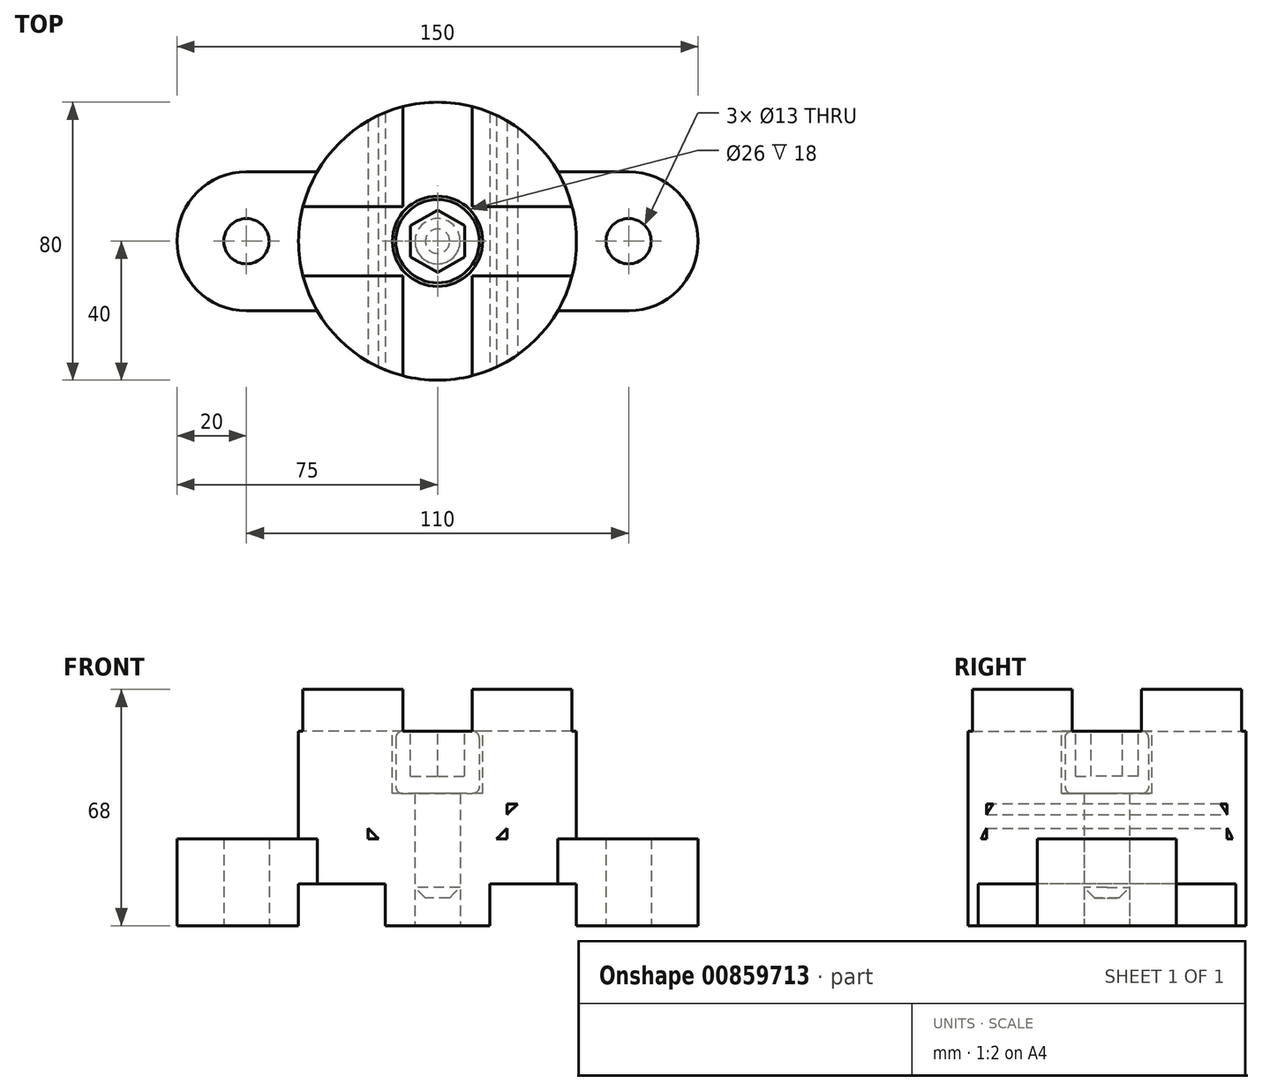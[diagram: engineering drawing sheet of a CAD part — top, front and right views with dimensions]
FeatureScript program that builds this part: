
annotation { "Feature Type Name" : "Feature", "Feature Type Description" : "" }
export const myFeature = defineFeature(function(context is Context, id is Id, definition is map)
    precondition{}
    {
        {
            var Q0;
            Q0=qCreatedBy(makeId("Top.planeOp"),FACE);
            var sketch = newSketch(context, id + "F0", { "sketchPlane" : qUnion([Q0])});
            skCircle(sketch, "E0", {"center": v(0, 0) * mm, "radius": 40 * mm});
            skArc(sketch, "E1", {"start": v(55, -20) * mm, "mid": v(75, 0) * mm, "end": v(55, 20) * mm});
            skArc(sketch, "E2", {"start": v(-55, 20) * mm, "mid": v(-75, 0) * mm, "end": v(-55, -20) * mm});
            skLineSegment(sketch, "E3", {"start": v(-55, 20) * mm, "end": v(55, 20) * mm});
            skLineSegment(sketch, "E4", {"start": v(-55, -20) * mm, "end": v(55, -20) * mm});
            skCircle(sketch, "E5", {"center": v(0, 0) * mm, "radius": 6.5 * mm});
            skCircle(sketch, "E6", {"center": v(-55, 0) * mm, "radius": 6.5 * mm});
            skCircle(sketch, "E7", {"center": v(55, 0) * mm, "radius": 6.5 * mm});
            skSolve(sketch);
        }
        {
            var Q0;
            {var subQ0=sQuery(id+"F0.wireOp",EDGE,"E4");var subQ1=sQuery(id+"F0.wireOp",EDGE,"E0");var subQ2=makeQuery(id+"F0.imprint","INTERSECT",VERTEX,{"disambiguationData":[OD(0.0)],"derivedFrom":[subQ1,subQ0]});Q0=makeQuery(id+"F0.imprint","IMPRINT",FACE,{"disambiguationData":[TD([[makeQuery(id+"F0.imprint","IMPRINT",EDGE,{"disambiguationData":[TD([[subQ2,-1.0]])],"derivedFrom":subQ1}),1.0]])]});}
            var Q1;
            Q1=makeQuery(id+"F0.imprint","IMPRINT",FACE,{"disambiguationData":[TD([[makeQuery(id+"F0.imprint","IMPRINT",EDGE,{"derivedFrom":sQuery(id+"F0.wireOp",EDGE,"E5")}),-1.0]])]});
            var Q2;
            {var subQ0=sQuery(id+"F0.wireOp",EDGE,"E3");var subQ1=sQuery(id+"F0.wireOp",EDGE,"E0");var subQ2=makeQuery(id+"F0.imprint","INTERSECT",VERTEX,{"disambiguationData":[OD(0.0)],"derivedFrom":[subQ1,subQ0]});Q2=makeQuery(id+"F0.imprint","IMPRINT",FACE,{"disambiguationData":[TD([[makeQuery(id+"F0.imprint","IMPRINT",EDGE,{"disambiguationData":[TD([[subQ2,1.0]])],"derivedFrom":subQ1}),1.0]])]});}
            extrude(context, id + "F1", {"entities" : qUnion([Q0, Q1, Q2]), "depth" : 35 * mm, "offsetDistance" : 25 * mm});
        }
        {
            var Q0;
            {var subQ1=sQuery(id+"F0.wireOp",EDGE,"E2");Q0=makeQuery(id+"F0.imprint","IMPRINT",FACE,{"disambiguationData":[TD([[makeQuery(id+"F0.imprint","IMPRINT",EDGE,{"derivedFrom":subQ1}),1.0]])]});}
            var Q1;
            {var subQ1=sQuery(id+"F0.wireOp",EDGE,"E1");Q1=makeQuery(id+"F0.imprint","IMPRINT",FACE,{"disambiguationData":[TD([[makeQuery(id+"F0.imprint","IMPRINT",EDGE,{"derivedFrom":subQ1}),1.0]])]});}
            extrude(context, id + "F2", {"entities" : qUnion([Q0, Q1]), "operationType" : NewBodyOperationType.ADD, "depth" : 25 * mm, "offsetDistance" : 25 * mm});
        }
        {
            var Q0;
            Q0=qCreatedBy(makeId("Front.planeOp"),FACE);
            var sketch = newSketch(context, id + "F3", { "sketchPlane" : qUnion([Q0])});
            skLineSegment(sketch, "E8.bottom", {"start": v(20, 35) * mm, "end": v(-20, 35) * mm});
            skLineSegment(sketch, "E8.top", {"start": v(20, 25) * mm, "end": v(-20, 25) * mm});
            skLineSegment(sketch, "E8.left", {"start": v(20, 35) * mm, "end": v(20, 25) * mm});
            skLineSegment(sketch, "E8.right", {"start": v(-20, 35) * mm, "end": v(-20, 25) * mm});
            skPoint(sketch, "E8.middle", {"position": v(0, 30) * mm});
            skLineSegment(sketch, "E9.bottom", {"start": v(-40, 0) * mm, "end": v(-15, 0) * mm});
            skLineSegment(sketch, "E9.top", {"start": v(-40, 12) * mm, "end": v(-15, 12) * mm});
            skLineSegment(sketch, "E9.left", {"start": v(-40, 0) * mm, "end": v(-40, 12) * mm});
            skLineSegment(sketch, "E9.right", {"start": v(-15, 0) * mm, "end": v(-15, 12) * mm});
            skLineSegment(sketch, "E10.bottom", {"start": v(15, 0) * mm, "end": v(40, 0) * mm});
            skLineSegment(sketch, "E10.top", {"start": v(15, 12) * mm, "end": v(40, 12) * mm});
            skLineSegment(sketch, "E10.left", {"start": v(15, 0) * mm, "end": v(15, 12) * mm});
            skLineSegment(sketch, "E10.right", {"start": v(40, 0) * mm, "end": v(40, 12) * mm});
            skSolve(sketch);
        }
        {
            var Q0;
            Q0 = qSketchRegion(id + "F3", true);
            extrude(context, id + "F4", {"entities" : qUnion([Q0]), "operationType" : NewBodyOperationType.REMOVE, "endBound" : BoundingType.SYMMETRIC, "oppositeDirection" : true, "depth" : 100 * mm, "offsetDistance" : 25 * mm});
        }
        {
            var Q0;
            Q0=makeQuery(id+"F4.boolean.opBoolean","COPY",EDGE,{"derivedFrom":makeQuery(id+"F4.opExtrude","SWEPT_EDGE",EDGE,{"disambiguationData":[OSD([sQuery(id+"F3.wireOp",EDGE,"E8.bottom"),sQuery(id+"F3.wireOp",EDGE,"E8.right")])]})});
            var Q1;
            Q1=makeQuery(id+"F4.boolean.opBoolean","COPY",EDGE,{"derivedFrom":makeQuery(id+"F4.opExtrude","SWEPT_EDGE",EDGE,{"disambiguationData":[OSD([sQuery(id+"F3.wireOp",EDGE,"E8.bottom"),sQuery(id+"F3.wireOp",EDGE,"E8.left")])]})});
            chamfer(context, id + "F5", {"entities" : qUnion([Q0, Q1]), "width" : 3 * mm, "tangentPropagation" : true});
        }
        {
            var Q0;
            Q0=makeQuery(id+"F4.boolean.opBoolean","COPY",FACE,{"derivedFrom":makeQuery(id+"F4.opExtrude","SWEPT_FACE",FACE,{"disambiguationData":[OSD([sQuery(id+"F3.wireOp",EDGE,"E8.top")])]})});
            var sketch = newSketch(context, id + "F6", { "sketchPlane" : qUnion([Q0])});
            skArc(sketch, "E11.0", {"start": v(20, 34.64) * mm, "mid": v(0, 40) * mm, "end": v(-20, 34.64) * mm});
            skCircle(sketch, "E11.1", {"center": v(0, 0) * mm, "radius": 6.5 * mm});
            skLineSegment(sketch, "E11.2", {"start": v(-20, 34.64) * mm, "end": v(-20, -34.64) * mm});
            skArc(sketch, "E11.3", {"start": v(-20, -34.64) * mm, "mid": v(0, -40) * mm, "end": v(20, -34.64) * mm});
            skLineSegment(sketch, "E11.4", {"start": v(20, 34.64) * mm, "end": v(20, -34.64) * mm});
            skSolve(sketch);
        }
        {
            var Q0;
            Q0 = qSketchRegion(id + "F6", true);
            var Q1;
            {var subQ0=sQuery(id+"F0.wireOp",EDGE,"E0");Q1=makeQuery(id+"F4.boolean.opBoolean","SPLIT",FACE,{"disambiguationData":[TD([makeQuery(id+"F4.opExtrude","SWEPT_FACE",FACE,{"disambiguationData":[OSD([sQuery(id+"F3.wireOp",EDGE,"E8.right")])]})])],"derivedFrom":makeQuery(id+"F1.opExtrude","CAP_FACE",FACE,{"disambiguationData":[OSD([subQ0,sQuery(id+"F0.wireOp",EDGE,"E5")])],"isStart":false})});}
            extrude(context, id + "F7", {"entities" : qUnion([Q0]), "endBound" : BoundingType.UP_TO_SURFACE, "depth" : 25 * mm, "endBoundEntityFace" : qUnion([Q1]), "offsetDistance" : 25 * mm});
        }
        {
            var Q0;
            Q0=makeQuery(id+"F7.opExtrude","CAP_EDGE",EDGE,{"disambiguationData":[OSD([sQuery(id+"F6.wireOp",EDGE,"E11.4")])],"isStart":true});
            var Q1;
            Q1=makeQuery(id+"F7.opExtrude","CAP_EDGE",EDGE,{"disambiguationData":[OSD([sQuery(id+"F6.wireOp",EDGE,"E11.2")])],"isStart":true});
            chamfer(context, id + "F8", {"entities" : qUnion([Q0, Q1]), "width" : 3 * mm, "tangentPropagation" : true});
        }
        {
            var Q0;
            Q0=makeQuery(id+"F7.opExtrude","CAP_FACE",FACE,{"disambiguationData":[OSD([sQuery(id+"F6.wireOp",EDGE,"E11.0"),sQuery(id+"F6.wireOp",EDGE,"E11.1"),sQuery(id+"F6.wireOp",EDGE,"E11.2"),sQuery(id+"F6.wireOp",EDGE,"E11.3"),sQuery(id+"F6.wireOp",EDGE,"E11.4")])],"isStart":false});
            var sketch = newSketch(context, id + "F9", { "sketchPlane" : qUnion([Q0])});
            skCircle(sketch, "E12", {"center": v(0, 0) * mm, "radius": 40 * mm});
            skSolve(sketch);
        }
        {
            var Q0;
            Q0 = qSketchRegion(id + "F9", true);
            extrude(context, id + "F10", {"entities" : qUnion([Q0]), "operationType" : NewBodyOperationType.ADD, "depth" : (45 - 12) * mm, "offsetDistance" : 25 * mm});
        }
        {
            var Q0;
            Q0=makeQuery(id+"F10.opExtrude","CAP_FACE",FACE,{"disambiguationData":[OSD([sQuery(id+"F9.wireOp",EDGE,"E12")])],"isStart":false});
            var sketch = newSketch(context, id + "F11", { "sketchPlane" : qUnion([Q0])});
            skCircle(sketch, "E13", {"center": v(0, 0) * mm, "radius": 13 * mm});
            skLineSegment(sketch, "E14.bottom", {"start": v(40, -10) * mm, "end": v(-40, -10) * mm});
            skLineSegment(sketch, "E14.top", {"start": v(40, 10) * mm, "end": v(-40, 10) * mm});
            skLineSegment(sketch, "E14.left", {"start": v(40, -10) * mm, "end": v(40, 10) * mm});
            skLineSegment(sketch, "E14.right", {"start": v(-40, -10) * mm, "end": v(-40, 10) * mm});
            skLineSegment(sketch, "E15.bottom", {"start": v(10, -40) * mm, "end": v(-10, -40) * mm});
            skLineSegment(sketch, "E15.top", {"start": v(10, 40) * mm, "end": v(-10, 40) * mm});
            skLineSegment(sketch, "E15.left", {"start": v(10, -40) * mm, "end": v(10, 40) * mm});
            skLineSegment(sketch, "E15.right", {"start": v(-10, -40) * mm, "end": v(-10, 40) * mm});
            skSolve(sketch);
        }
        {
            var Q0;
            {var subQ0=sQuery(id+"F11.wireOp",EDGE,"E14.top");var subQ1=sQuery(id+"F11.wireOp",EDGE,"E13");var subQ2=makeQuery(id+"F11.imprint","INTERSECT",VERTEX,{"disambiguationData":[OD(0.0)],"derivedFrom":[subQ1,subQ0]});Q0=makeQuery(id+"F11.imprint","IMPRINT",FACE,{"disambiguationData":[TD([[makeQuery(id+"F11.imprint","IMPRINT",EDGE,{"disambiguationData":[TD([[subQ2,-1.0]])],"derivedFrom":subQ1}),1.0]])]});}
            var Q1;
            {var subQ1=sQuery(id+"F11.wireOp",EDGE,"E13");var subQ8=sQuery(id+"F11.wireOp",EDGE,"E14.top");var subQ11=makeQuery(id+"F11.imprint","INTERSECT",VERTEX,{"disambiguationData":[OD(0.0)],"derivedFrom":[subQ1,subQ8]});Q1=makeQuery(id+"F11.imprint","IMPRINT",FACE,{"disambiguationData":[TD([[makeQuery(id+"F11.imprint","IMPRINT",EDGE,{"disambiguationData":[TD([[subQ11,1.0]])],"derivedFrom":subQ1}),1.0]])]});}
            var Q2;
            {var subQ0=sQuery(id+"F11.wireOp",EDGE,"E15.right");var subQ1=sQuery(id+"F11.wireOp",EDGE,"E13");var subQ2=makeQuery(id+"F11.imprint","INTERSECT",VERTEX,{"disambiguationData":[OD(0.0)],"derivedFrom":[subQ1,subQ0]});Q2=makeQuery(id+"F11.imprint","IMPRINT",FACE,{"disambiguationData":[TD([[makeQuery(id+"F11.imprint","IMPRINT",EDGE,{"disambiguationData":[TD([[subQ2,-1.0]])],"derivedFrom":subQ1}),1.0]])]});}
            var Q3;
            {var subQ0=sQuery(id+"F11.wireOp",EDGE,"E14.bottom");var subQ1=sQuery(id+"F11.wireOp",EDGE,"E13");var subQ2=makeQuery(id+"F11.imprint","INTERSECT",VERTEX,{"disambiguationData":[OD(0.0)],"derivedFrom":[subQ1,subQ0]});Q3=makeQuery(id+"F11.imprint","IMPRINT",FACE,{"disambiguationData":[TD([[makeQuery(id+"F11.imprint","IMPRINT",EDGE,{"disambiguationData":[TD([[subQ2,-1.0]])],"derivedFrom":subQ1}),1.0]])]});}
            var Q4;
            {var subQ0=sQuery(id+"F11.wireOp",EDGE,"E15.left");var subQ1=sQuery(id+"F11.wireOp",EDGE,"E13");var subQ2=makeQuery(id+"F11.imprint","INTERSECT",VERTEX,{"disambiguationData":[OD(0.0)],"derivedFrom":[subQ1,subQ0]});Q4=makeQuery(id+"F11.imprint","IMPRINT",FACE,{"disambiguationData":[TD([[makeQuery(id+"F11.imprint","IMPRINT",EDGE,{"disambiguationData":[TD([[subQ2,1.0]])],"derivedFrom":subQ1}),1.0]])]});}
            extrude(context, id + "F12", {"entities" : qUnion([Q0, Q1, Q2, Q3, Q4]), "operationType" : NewBodyOperationType.REMOVE, "oppositeDirection" : true, "depth" : 30 * mm, "offsetDistance" : 25 * mm});
        }
        {
            var Q0;
            {var subQ1=sQuery(id+"F11.wireOp",EDGE,"E14.top");var subQ5=sQuery(id+"F11.wireOp",EDGE,"E13");var subQ9=makeQuery(id+"F11.imprint","INTERSECT",VERTEX,{"disambiguationData":[OD(0.0)],"derivedFrom":[subQ5,subQ1]});Q0=makeQuery(id+"F11.imprint","IMPRINT",FACE,{"disambiguationData":[TD([[makeQuery(id+"F11.imprint","IMPRINT",EDGE,{"disambiguationData":[TD([[subQ9,-1.0]])],"derivedFrom":subQ5}),-1.0]])]});}
            var Q1;
            {var subQ0=sQuery(id+"F11.wireOp",EDGE,"E15.right");var subQ1=sQuery(id+"F11.wireOp",EDGE,"E13");var subQ10=makeQuery(id+"F11.imprint","INTERSECT",VERTEX,{"disambiguationData":[OD(0.0)],"derivedFrom":[subQ1,subQ0]});Q1=makeQuery(id+"F11.imprint","IMPRINT",FACE,{"disambiguationData":[TD([[makeQuery(id+"F11.imprint","IMPRINT",EDGE,{"disambiguationData":[TD([[subQ10,-1.0]])],"derivedFrom":subQ1}),-1.0]])]});}
            var Q2;
            {var subQ0=sQuery(id+"F11.wireOp",EDGE,"E14.top");var subQ1=sQuery(id+"F11.wireOp",EDGE,"E13");var subQ2=makeQuery(id+"F11.imprint","INTERSECT",VERTEX,{"disambiguationData":[OD(1.0)],"derivedFrom":[subQ1,subQ0]});Q2=makeQuery(id+"F11.imprint","IMPRINT",FACE,{"disambiguationData":[TD([[makeQuery(id+"F11.imprint","IMPRINT",EDGE,{"disambiguationData":[TD([[subQ2,-1.0]])],"derivedFrom":subQ1}),-1.0]])]});}
            var Q3;
            {var subQ0=sQuery(id+"F11.wireOp",EDGE,"E14.top");var subQ1=sQuery(id+"F11.wireOp",EDGE,"E13");var subQ2=makeQuery(id+"F11.imprint","INTERSECT",VERTEX,{"disambiguationData":[OD(0.0)],"derivedFrom":[subQ1,subQ0]});Q3=makeQuery(id+"F11.imprint","IMPRINT",FACE,{"disambiguationData":[TD([[makeQuery(id+"F11.imprint","IMPRINT",EDGE,{"disambiguationData":[TD([[subQ2,1.0]])],"derivedFrom":subQ1}),-1.0]])]});}
            var Q4;
            {var subQ0=sQuery(id+"F11.wireOp",EDGE,"E15.left");var subQ8=sQuery(id+"F11.wireOp",EDGE,"E13");var subQ10=makeQuery(id+"F11.imprint","INTERSECT",VERTEX,{"disambiguationData":[OD(0.0)],"derivedFrom":[subQ8,subQ0]});Q4=makeQuery(id+"F11.imprint","IMPRINT",FACE,{"disambiguationData":[TD([[makeQuery(id+"F11.imprint","IMPRINT",EDGE,{"disambiguationData":[TD([[subQ10,1.0]])],"derivedFrom":subQ8}),-1.0]])]});}
            var Q5;
            {var subQ0=sQuery(id+"F11.wireOp",EDGE,"E14.bottom");var subQ1=sQuery(id+"F11.wireOp",EDGE,"E13");var subQ2=makeQuery(id+"F11.imprint","INTERSECT",VERTEX,{"disambiguationData":[OD(1.0)],"derivedFrom":[subQ1,subQ0]});Q5=makeQuery(id+"F11.imprint","IMPRINT",FACE,{"disambiguationData":[TD([[makeQuery(id+"F11.imprint","IMPRINT",EDGE,{"disambiguationData":[TD([[subQ2,-1.0]])],"derivedFrom":subQ1}),-1.0]])]});}
            var Q6;
            {var subQ1=sQuery(id+"F11.wireOp",EDGE,"E14.bottom");var subQ8=sQuery(id+"F11.wireOp",EDGE,"E13");var subQ9=makeQuery(id+"F11.imprint","INTERSECT",VERTEX,{"disambiguationData":[OD(0.0)],"derivedFrom":[subQ8,subQ1]});Q6=makeQuery(id+"F11.imprint","IMPRINT",FACE,{"disambiguationData":[TD([[makeQuery(id+"F11.imprint","IMPRINT",EDGE,{"disambiguationData":[TD([[subQ9,-1.0]])],"derivedFrom":subQ8}),-1.0]])]});}
            var Q7;
            {var subQ0=sQuery(id+"F11.wireOp",EDGE,"E15.right");var subQ1=sQuery(id+"F11.wireOp",EDGE,"E13");var subQ2=makeQuery(id+"F11.imprint","INTERSECT",VERTEX,{"disambiguationData":[OD(1.0)],"derivedFrom":[subQ1,subQ0]});Q7=makeQuery(id+"F11.imprint","IMPRINT",FACE,{"disambiguationData":[TD([[makeQuery(id+"F11.imprint","IMPRINT",EDGE,{"disambiguationData":[TD([[subQ2,-1.0]])],"derivedFrom":subQ1}),-1.0]])]});}
            extrude(context, id + "F13", {"entities" : qUnion([Q0, Q1, Q2, Q3, Q4, Q5, Q6, Q7]), "operationType" : NewBodyOperationType.REMOVE, "oppositeDirection" : true, "depth" : 12 * mm, "offsetDistance" : 25 * mm});
        }
        {
            var Q0;
            Q0=makeQuery(id+"F10.boolean.opBoolean","SPLIT",FACE,{"disambiguationData":[TD([makeQuery(id+"F7.opExtrude","SWEPT_FACE",FACE,{"disambiguationData":[OSD([sQuery(id+"F6.wireOp",EDGE,"E11.1")])]})])],"derivedFrom":makeQuery(id+"F10.opExtrude","CAP_FACE",FACE,{"disambiguationData":[OSD([sQuery(id+"F9.wireOp",EDGE,"E12")])],"isStart":true})});
            extrude(context, id + "F14", {"entities" : qUnion([Q0]), "operationType" : NewBodyOperationType.REMOVE, "endBound" : BoundingType.THROUGH_ALL, "oppositeDirection" : true, "depth" : 25 * mm, "offsetDistance" : 25 * mm});
        }
        {
            var Q0;
            Q0=qCreatedBy(makeId("Front.planeOp"),FACE);
            var sketch = newSketch(context, id + "F15", { "sketchPlane" : qUnion([Q0])});
            skLineSegment(sketch, "E16", {"start": v(0, 56) * mm, "end": v(10, 56) * mm});
            skLineSegment(sketch, "E17", {"start": v(12, 54) * mm, "end": v(12, 40) * mm});
            skLineSegment(sketch, "E18", {"start": v(10, 38) * mm, "end": v(6.5, 38) * mm});
            skLineSegment(sketch, "E19", {"start": v(6.5, 38) * mm, "end": v(6.5, 8) * mm});
            skLineSegment(sketch, "E20", {"start": v(6.5, 8) * mm, "end": v(0, 8) * mm});
            skLineSegment(sketch, "E21", {"start": v(0, 8) * mm, "end": v(0, 56) * mm});
            skPoint(sketch, "E22.visualSharp", {"position": v(12, 56) * mm});
            skArc(sketch, "E22.filletArc", {"start": v(12, 54) * mm, "mid": v(11.41, 55.41) * mm, "end": v(10, 56) * mm});
            skPoint(sketch, "E23.visualSharp", {"position": v(12, 38) * mm});
            skArc(sketch, "E23.filletArc", {"start": v(10, 38) * mm, "mid": v(11.41, 38.59) * mm, "end": v(12, 40) * mm});
            skSolve(sketch);
        }
        {
            var Q0;
            Q0=makeQuery(id+"F15.imprint","IMPRINT",FACE,{"disambiguationData":[TD([[makeQuery(id+"F15.imprint","IMPRINT",EDGE,{"derivedFrom":sQuery(id+"F15.wireOp",EDGE,"E16")}),-1.0]])]});
            var Q1;
            Q1=sQuery(id+"F15.wireOp",EDGE,"E21");
            revolve(context, id + "F16", {"surfaceOperationType" : NewSurfaceOperationType.NEW, "entities" : qUnion([Q0]), "axis" : qUnion([Q1]), "revolveType" : RevolveType.FULL});
        }
        {
            var Q0;
            Q0=makeQuery(id+"F16.opRevolve","SWEPT_EDGE",EDGE,{"disambiguationData":[OSD([sQuery(id+"F15.wireOp",EDGE,"E19"),sQuery(id+"F15.wireOp",EDGE,"E20")])]});
            chamfer(context, id + "F17", {"entities" : qUnion([Q0]), "width" : 3 * mm, "tangentPropagation" : true});
        }
        {
            var Q0;
            Q0=makeQuery(id+"F16.opRevolve","SWEPT_FACE",FACE,{"disambiguationData":[OSD([sQuery(id+"F15.wireOp",EDGE,"E16")])]});
            var sketch = newSketch(context, id + "F18", { "sketchPlane" : qUnion([Q0])});
            skCircle(sketch, "E24.cCircle", {"center": v(0, 0) * mm, "radius": 7.8 * mm, "construction": true});
            skLineSegment(sketch, "E24.0", {"start": v(7.8, 4.5) * mm, "end": v(7.8, -4.5) * mm});
            skLineSegment(sketch, "E24.1", {"start": v(7.8, -4.5) * mm, "end": v(0, -9) * mm});
            skLineSegment(sketch, "E24.2", {"start": v(0, -9) * mm, "end": v(-7.8, -4.5) * mm});
            skLineSegment(sketch, "E24.3", {"start": v(-7.8, -4.5) * mm, "end": v(-7.8, 4.5) * mm});
            skLineSegment(sketch, "E24.4", {"start": v(-7.8, 4.5) * mm, "end": v(0, 9) * mm});
            skLineSegment(sketch, "E24.5", {"start": v(0, 9) * mm, "end": v(7.8, 4.5) * mm});
            skPoint(sketch, "E24.0.midPoint", {"position": v(7.8, 0) * mm});
            skSolve(sketch);
        }
        {
            var Q0;
            Q0 = qSketchRegion(id + "F18", true);
            extrude(context, id + "F19", {"entities" : qUnion([Q0]), "operationType" : NewBodyOperationType.REMOVE, "oppositeDirection" : true, "depth" : 13 * mm, "offsetDistance" : 25 * mm});
        }
    });
